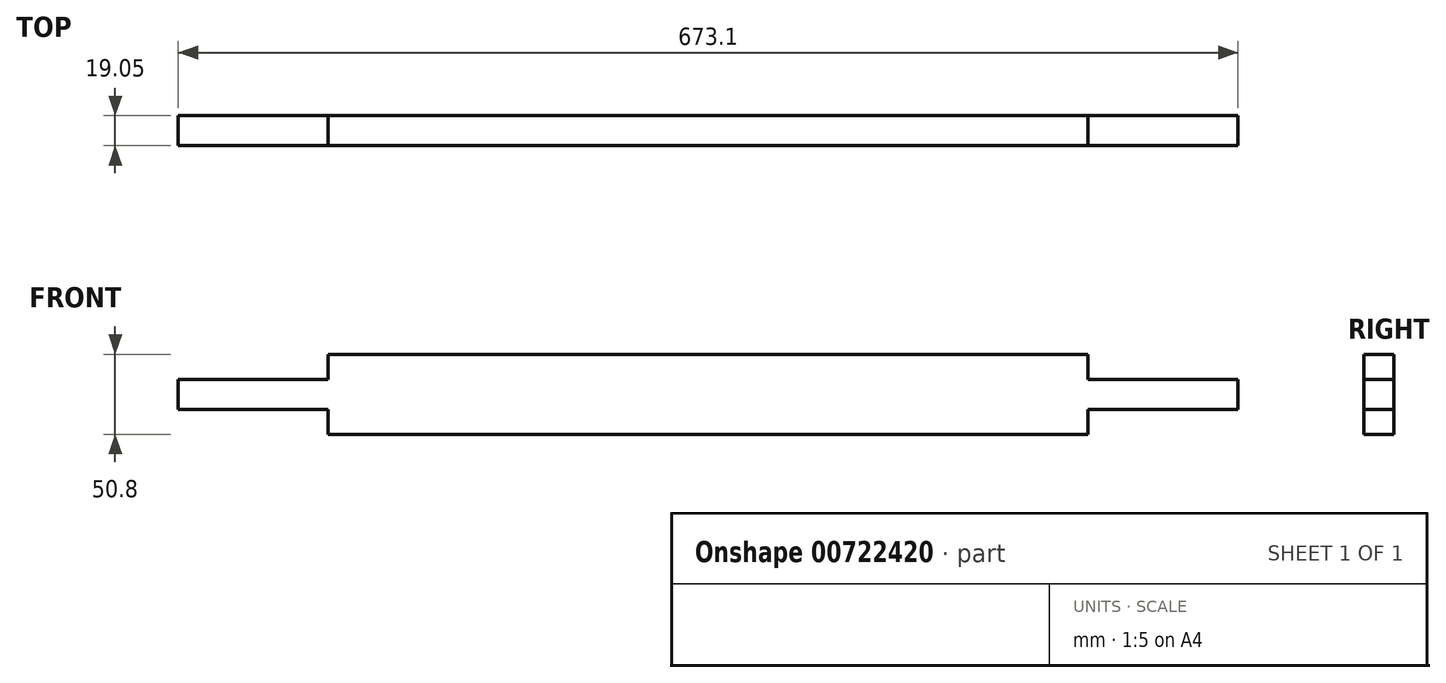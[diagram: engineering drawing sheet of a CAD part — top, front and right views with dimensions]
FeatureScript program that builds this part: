
annotation { "Feature Type Name" : "Feature", "Feature Type Description" : "" }
export const myFeature = defineFeature(function(context is Context, id is Id, definition is map)
    precondition{}
    {
        {
            var Q0;
            Q0=qCreatedBy(makeId("Front.planeOp"),FACE);
            var sketch = newSketch(context, id + "F0", { "sketchPlane" : qUnion([Q0])});
            skLineSegment(sketch, "E0.bottom", {"start": v(336.55, -25.4) * mm, "end": v(-336.55, -25.4) * mm});
            skLineSegment(sketch, "E0.top", {"start": v(336.55, 25.4) * mm, "end": v(-336.55, 25.4) * mm});
            skLineSegment(sketch, "E0.left", {"start": v(336.55, -25.4) * mm, "end": v(336.55, 25.4) * mm});
            skLineSegment(sketch, "E0.right", {"start": v(-336.55, -25.4) * mm, "end": v(-336.55, 25.4) * mm});
            skPoint(sketch, "E0.middle", {"position": v(0, 0) * mm});
            skLineSegment(sketch, "E1.bottom", {"start": v(-336.55, 25.4) * mm, "end": v(-241.3, 25.4) * mm});
            skLineSegment(sketch, "E1.top", {"start": v(-336.55, 9.52) * mm, "end": v(-241.3, 9.52) * mm});
            skLineSegment(sketch, "E1.left", {"start": v(-336.55, 25.4) * mm, "end": v(-336.55, 9.52) * mm});
            skLineSegment(sketch, "E1.right", {"start": v(-241.3, 25.4) * mm, "end": v(-241.3, 9.52) * mm});
            skLineSegment(sketch, "E2.bottom", {"start": v(-336.55, -25.4) * mm, "end": v(-241.3, -25.4) * mm});
            skLineSegment(sketch, "E2.top", {"start": v(-336.55, -9.53) * mm, "end": v(-241.3, -9.53) * mm});
            skLineSegment(sketch, "E2.left", {"start": v(-336.55, -25.4) * mm, "end": v(-336.55, -9.53) * mm});
            skLineSegment(sketch, "E2.right", {"start": v(-241.3, -25.4) * mm, "end": v(-241.3, -9.53) * mm});
            skLineSegment(sketch, "E3.bottom", {"start": v(336.55, -25.4) * mm, "end": v(241.3, -25.4) * mm});
            skLineSegment(sketch, "E3.top", {"start": v(336.55, -9.53) * mm, "end": v(241.3, -9.53) * mm});
            skLineSegment(sketch, "E3.left", {"start": v(336.55, -25.4) * mm, "end": v(336.55, -9.53) * mm});
            skLineSegment(sketch, "E3.right", {"start": v(241.3, -25.4) * mm, "end": v(241.3, -9.53) * mm});
            skLineSegment(sketch, "E4.bottom", {"start": v(336.55, 25.4) * mm, "end": v(241.3, 25.4) * mm});
            skLineSegment(sketch, "E4.top", {"start": v(336.55, 9.52) * mm, "end": v(241.3, 9.52) * mm});
            skLineSegment(sketch, "E4.left", {"start": v(336.55, 25.4) * mm, "end": v(336.55, 9.52) * mm});
            skLineSegment(sketch, "E4.right", {"start": v(241.3, 25.4) * mm, "end": v(241.3, 9.52) * mm});
            skSolve(sketch);
        }
        {
            var Q0;
            {var subQ3=sQuery(id+"F0.wireOp",EDGE,"E1.top");Q0=makeQuery(id+"F0.imprint","IMPRINT",FACE,{"disambiguationData":[TD([[makeQuery(id+"F0.imprint","IMPRINT",EDGE,{"derivedFrom":subQ3}),-1.0]])]});}
            extrude(context, id + "F1", {"entities" : qUnion([Q0]), "depth" : 19.05 * mm, "offsetDistance" : 25.4 * mm});
        }
    });
